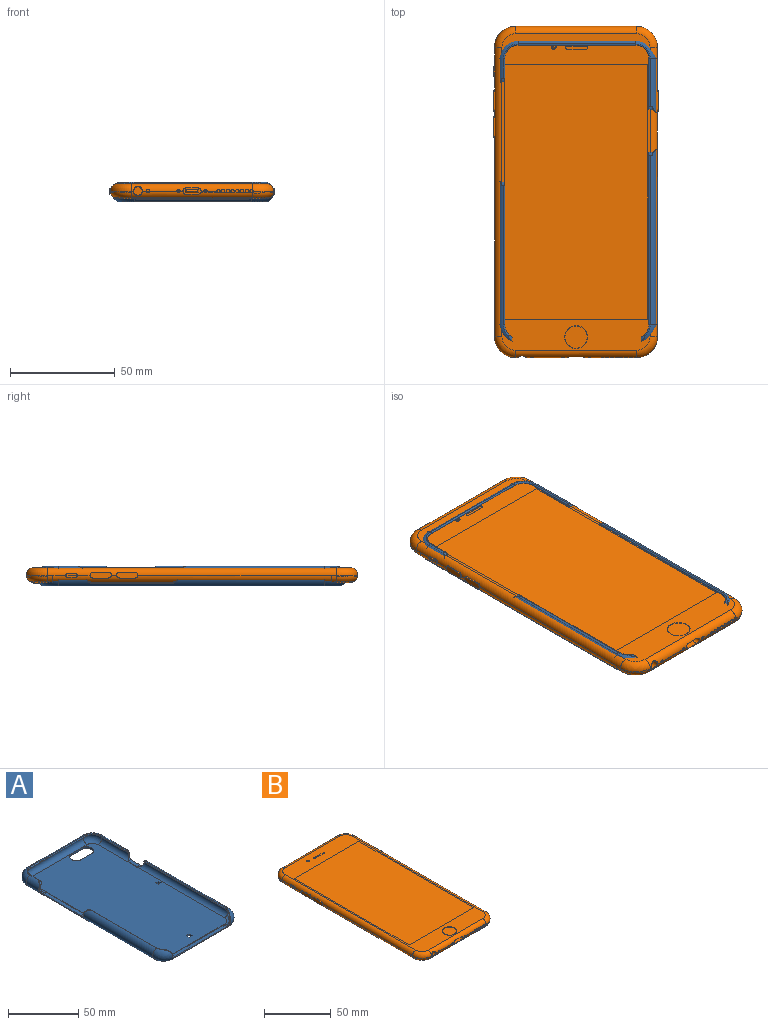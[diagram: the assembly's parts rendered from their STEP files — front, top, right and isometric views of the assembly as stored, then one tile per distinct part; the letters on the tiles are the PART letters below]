
ASSEMBLY  parts=2 mates=1
PART A: 103 faces, bbox 79x150.1x9.5 mm
  f0: cylinder r=3.5mm len=127.1mm, axis (0,1,0), area 1149.3mm2, adj f1,f8,f14,f16,f26,f53,f54,f55
  f1: cylinder r=0.5mm len=82.87mm, axis (0,1,0), area 128mm2, adj f0,f9,f15,f59,f60
  f2: cylinder r=3.5mm len=127.1mm, axis (0,1,0), area 873.9mm2, adj f3,f5,f11,f22,f26,f27,f28,f42
  f3: cylinder r=0.5mm len=11.42mm, axis (0,1,0), area 15.6mm2, adj f2,f4,f23,f46,f51
  f4: cylinder r=5mm len=127.1mm, axis (0,1,0), area 1097.8mm2, adj f3,f13,f24,f25,f27,f51,f52,f84
  f5: plane 16.43x0mm, normal (1,0,0), area 0.1mm2, adj f2,f26,f42
  f6: cylinder r=3.5mm len=56mm, axis (1,0,0), area 26.2mm2, adj f8,f11,f26,f31,f34,f35,f40,f41
  f7: cylinder r=5mm len=56mm, axis (1,0,0), area 114.5mm2, adj f10,f13,f25,f71,f72,f73
  f8: torus R=5.74mm, axis (0,0,1), area 122.4mm2, adj f0,f6,f9,f26,f29,f30,f31
  f9: torus R=6.88mm, axis (0,0,1), area 10.2mm2, adj f1,f8,f10,f29,f32,f33
  f10: torus R=5.6mm, axis (0,0,1), area 165.3mm2, adj f7,f9,f15,f25,f32,f74,f75,f76
  f11: torus R=5.74mm, axis (0,0,1), area 122.4mm2, adj f2,f6,f12,f26,f35,f36,f37
  f12: torus R=6.88mm, axis (0,0,1), area 10.2mm2, adj f11,f13,f27,f37,f38,f39
  f13: torus R=5.6mm, axis (0,0,1), area 165.3mm2, adj f4,f7,f12,f25,f38,f68,f69,f70
  f14: cylinder r=0.5mm len=24.73mm, axis (0,1,0), area 36.6mm2, adj f0,f15,f17,f53,f61
  f15: cylinder r=5mm len=127.1mm, axis (0,1,0), area 1384.9mm2, adj f1,f10,f14,f18,f25,f60,f61,f77
  f16: torus R=5.74mm, axis (0,0,1), area 129.9mm2, adj f0,f17,f19,f26
  f17: torus R=6.88mm, axis (0,0,1), area 16.2mm2, adj f14,f16,f18,f20
  f18: torus R=5.6mm, axis (0,0,1), area 182mm2, adj f15,f17,f21,f25
  f19: cylinder r=3.5mm len=56mm, axis (-1,0,0), area 572.6mm2, adj f16,f20,f22,f26,f64
  f20: cylinder r=0.5mm len=56mm, axis (-1,0,0), area 88mm2, adj f17,f19,f21,f23
  f21: cylinder r=5mm len=56mm, axis (-1,0,0), area 688.9mm2, adj f18,f20,f24,f25
  f22: torus R=5.74mm, axis (0,0,1), area 129.9mm2, adj f2,f19,f23,f26
  f23: torus R=6.88mm, axis (0,0,1), area 16.2mm2, adj f3,f20,f22,f24
  f24: torus R=5.6mm, axis (0,0,1), area 182mm2, adj f4,f21,f23,f25
  f25: plane 142.1x71mm, normal (0,0,-1), area 9834.1mm2, adj f4,f7,f10,f13,f15,f18,f21,f24
  f26: plane 138.18x67.14mm, normal (0,0,1), area 9026.4mm2, adj f0,f2,f5,f6,f8,f11,f16,f19
  f27: cylinder r=0.5mm len=68.7mm, axis (0,1,0), area 105.6mm2, adj f2,f4,f12,f47,f52
  f28: plane 73.67x0mm, normal (1,0,0), area 0.3mm2, adj f2,f26,f43
  f29: cylinder r=3.5mm len=4.97mm, axis (0,1,0), area 7.4mm2, adj f8,f9,f30,f32,f33,f76
  f30: plane 1.06x0.55mm, normal (-1,0,0), area 0.5mm2, adj f8,f29,f31,f75
  f31: cylinder r=3.5mm len=4.29mm, axis (0,1,0), area 9.6mm2, adj f6,f8,f30,f34,f73,f74
  f32: plane 1.34x0.37mm, normal (-1,0,0), area 0.2mm2, adj f9,f10,f29,f33,f76
  f33: plane 0.66x0.4mm, normal (0,-1,0), area 0.1mm2, adj f9,f29,f32
  f34: plane 50.8x3.01mm, normal (0,0,1), area 152.9mm2, adj f6,f31,f35,f72
  f35: cylinder r=3.5mm len=4.29mm, axis (0,1,0), area 9.6mm2, adj f6,f11,f34,f36,f70,f71
  f36: plane 1.06x0.55mm, normal (1,0,0), area 0.5mm2, adj f11,f35,f37,f69
  f37: cylinder r=3.5mm len=4.97mm, axis (0,1,0), area 7.4mm2, adj f11,f12,f36,f38,f39,f68
  f38: plane 1.34x0.37mm, normal (1,0,0), area 0.2mm2, adj f12,f13,f37,f39,f68
  f39: plane 0.66x0.4mm, normal (0,-1,0), area 0.1mm2, adj f12,f37,f38
  f40: cylinder r=3.5mm len=0.17mm, axis (0,1,0), area 0mm2, adj f6,f26
  f41: cylinder r=3.5mm len=0.17mm, axis (0,1,0), area 0mm2, adj f6,f26
  f42: cylinder r=3.5mm len=0.17mm, axis (-1,0,0), area 0mm2, adj f2,f5,f26
  f43: cylinder r=3.5mm len=0.17mm, axis (-1,0,0), area 0mm2, adj f2,f26,f28
  f44: plane 37x3.01mm, normal (0,0,1), area 111.4mm2, adj f2,f49,f50,f87
  f45: plane 1.06x0.47mm, normal (0,-1,0), area 0.5mm2, adj f2,f46,f49,f89
  f46: cylinder r=3.5mm len=3.8mm, axis (-1,0,0), area 8.6mm2, adj f2,f3,f45,f51,f90
  f47: cylinder r=3.5mm len=3.8mm, axis (-1,0,0), area 8.6mm2, adj f2,f27,f48,f52,f84
  f48: plane 1.09x0.97mm, normal (0,1,0), area 1mm2, adj f2,f47,f50,f85
  f49: cylinder r=3.5mm len=4.36mm, axis (-1,0,0), area 8.9mm2, adj f2,f44,f45,f88
  f50: cylinder r=3.5mm len=4.38mm, axis (-1,0,0), area 10.2mm2, adj f2,f44,f48,f86
  f51: plane 1.53x0.39mm, normal (0,-1,0), area 0.3mm2, adj f3,f4,f46,f90
  f52: plane 1.53x0.39mm, normal (0,1,0), area 0.3mm2, adj f4,f27,f47,f84
  f53: cylinder r=3.5mm len=3.85mm, axis (1,0,0), area 9mm2, adj f0,f14,f54,f61,f77
  f54: plane 1.05x0.32mm, normal (0,-1,0), area 0.3mm2, adj f0,f53,f55,f78
  f55: cylinder r=3.5mm len=4.36mm, axis (1,0,0), area 8.9mm2, adj f0,f54,f56,f79
  f56: plane 9x3.01mm, normal (0,0,1), area 27.1mm2, adj f0,f55,f57,f80
  f57: cylinder r=3.5mm len=4.36mm, axis (1,0,0), area 8.9mm2, adj f0,f56,f58,f81
  f58: plane 1.05x0.32mm, normal (0,1,0), area 0.3mm2, adj f0,f57,f59,f82
  f59: cylinder r=3.5mm len=3.85mm, axis (1,0,0), area 9mm2, adj f0,f1,f58,f60,f83
  f60: plane 1.84x0.56mm, normal (0,1,0), area 0.6mm2, adj f1,f15,f59,f83
  f61: plane 1.84x0.56mm, normal (0,-1,0), area 0.6mm2, adj f14,f15,f53,f77
  f62: cylinder r=3.5mm len=0.17mm, axis (1,0,0), area 0mm2, adj f0,f26
  f63: cylinder r=3.5mm len=0.17mm, axis (1,0,0), area 0mm2, adj f0,f26
  f64: plane 10.12x1.61mm, normal (0,-1,0), area 16.2mm2, adj f19,f25,f65,f67
  f65: cylinder r=5mm len=10mm, axis (0,0,1), area 25.1mm2, adj f25,f26,f64,f66
  f66: plane 10.11x1.6mm, normal (0,1,0), area 16.2mm2, adj f25,f26,f65,f67
  f67: cylinder r=5mm len=10mm, axis (0,0,1), area 25.1mm2, adj f25,f26,f64,f66
  f68: bspline ~4.29x3.86mm, area 2.1mm2, adj f13,f37,f38,f69
  f69: bspline ~0.6x0.38mm, area 0.2mm2, adj f13,f36,f68,f70
  f70: bspline ~2.94x1.44mm, area 1.4mm2, adj f13,f35,f69,f71
  f71: bspline ~2.6x1.46mm, area 1.5mm2, adj f7,f35,f70,f72
  f72: plane 50.8x0.51mm, normal (0,-0.92,0.38), area 28mm2, adj f7,f34,f71,f73
  f73: bspline ~2.6x1.46mm, area 1.5mm2, adj f7,f31,f72,f74
  f74: bspline ~2.94x1.45mm, area 1.4mm2, adj f10,f31,f73,f75
  f75: bspline ~0.6x0.38mm, area 0.2mm2, adj f10,f30,f74,f76
  f76: bspline ~4.29x3.86mm, area 2.1mm2, adj f10,f29,f32,f75
  f77: bspline ~3.8x3.54mm, area 1.8mm2, adj f15,f53,f61,f78
  f78: cone r=4.7mm half-angle=45deg, axis (0,1,0), area 0.1mm2, adj f15,f54,f77,f79
  f79: bspline ~4.04x3.8mm, area 2.9mm2, adj f15,f55,f78,f80
  f80: plane 9x0.51mm, normal (0.92,0,0.38), area 5mm2, adj f15,f56,f79,f81
  f81: bspline ~4.04x3.8mm, area 2.9mm2, adj f15,f57,f80,f82
  f82: cone r=4.7mm half-angle=45deg, axis (0,-1,0), area 0.1mm2, adj f15,f58,f81,f83
  f83: bspline ~3.5x3.5mm, area 1.8mm2, adj f15,f59,f60,f82
  f84: bspline ~3.81x3.54mm, area 1.7mm2, adj f4,f47,f52,f85
  f85: cone r=5mm half-angle=45deg, axis (0,-1,0), area 0.4mm2, adj f4,f48,f84,f86
  f86: bspline ~3.79x3.79mm, area 2.7mm2, adj f4,f50,f85,f87
  f87: plane 37x0.51mm, normal (-0.92,0,0.38), area 20.4mm2, adj f4,f44,f86,f88
  f88: bspline ~4.04x3.8mm, area 2.9mm2, adj f4,f49,f87,f89
  f89: cone r=5mm half-angle=45deg, axis (0,1,0), area 0.2mm2, adj f4,f45,f88,f90
  f90: bspline ~3.81x3.54mm, area 1.7mm2, adj f4,f46,f51,f89
  f91: plane 3x1.6mm, normal (0,-1,0), area 4.8mm2, adj f25,f26,f92,f93
  f92: plane 3x1.6mm, normal (-1,0,0), area 4.8mm2, adj f25,f26,f91,f94
  f93: plane 3x1.6mm, normal (1,0,0), area 4.8mm2, adj f25,f26,f91,f94
  f94: plane 3x1.6mm, normal (0,1,0), area 4.8mm2, adj f25,f26,f92,f93
  f95: plane 3x1.6mm, normal (0,-1,0), area 4.8mm2, adj f25,f26,f96,f97
  f96: plane 3x1.6mm, normal (-1,0,0), area 4.8mm2, adj f25,f26,f95,f98
  f97: plane 3x1.6mm, normal (1,0,0), area 4.8mm2, adj f25,f26,f95,f98
  f98: plane 3x1.6mm, normal (0,1,0), area 4.8mm2, adj f25,f26,f96,f97
  f99: plane 3x1.6mm, normal (-1,0,0), area 4.8mm2, adj f25,f26,f100,f101
  f100: plane 3x1.6mm, normal (0,1,0), area 4.8mm2, adj f25,f26,f99,f102
  f101: plane 3x1.6mm, normal (0,-1,0), area 4.8mm2, adj f25,f26,f99,f102
  f102: plane 3x1.6mm, normal (1,0,0), area 4.8mm2, adj f25,f26,f100,f101
PART B: 184 faces, bbox 79.4x159.7x7.8 mm
  f0: cylinder r=3.55mm len=3.55mm, axis (0,1,0), area 12.2mm2, adj f2,f5,f6,f32,f62
  f1: cylinder r=3.55mm len=3.55mm, axis (0,-1,0), area 12.2mm2, adj f2,f4,f7,f36,f59
  f2: plane 70.69x1.5mm, normal (0,0,-1), area 106mm2, adj f0,f1,f8,f39
  f3: cylinder r=3.55mm len=57.79mm, axis (-1,0,0), area 154.9mm2, adj f4,f5,f9,f10,f11,f12,f13,f14
  f4: torus R=6.45mm, axis (0,0,-1), area 41.5mm2, adj f1,f3,f22,f23,f49,f50
  f5: torus R=6.45mm, axis (0,0,-1), area 42.1mm2, adj f0,f3,f24,f25,f69
  f6: cylinder r=3.55mm len=132.83mm, axis (0,1,0), area 710.8mm2, adj f0,f8,f28,f62,f78,f79,f81,f83
  f7: cylinder r=3.55mm len=132.83mm, axis (0,-1,0), area 709.9mm2, adj f1,f8,f27,f59,f74,f99,f100,f101
  f8: plane 132.83x70.69mm, normal (0,0,-1), area 9132.5mm2, adj f2,f6,f7,f26,f48,f65
  f9: cylinder r=3.55mm len=0.95mm, axis (-1,0,0), area 0.1mm2, adj f3,f43,f148
  f10: cylinder r=3.55mm len=2mm, axis (-1,0,0), area 0.4mm2, adj f3,f43,f56,f148
  f11: cylinder r=3.55mm len=13.09mm, axis (-1,0,0), area 4.2mm2, adj f3,f40,f43,f56
  f12: cylinder r=3.55mm len=1.41mm, axis (-1,0,0), area 0.5mm2, adj f3,f40,f43,f109
  f13: cylinder r=3.55mm len=1.49mm, axis (-1,0,0), area 0.7mm2, adj f3,f43,f44,f111
  f14: cylinder r=3.55mm len=5.01mm, axis (-1,0,0), area 2.5mm2, adj f3,f43,f44,f131
  f15: cylinder r=3.55mm len=1.06mm, axis (-1,0,0), area 0.5mm2, adj f3,f43,f129,f131
  f16: cylinder r=3.55mm len=1.09mm, axis (-1,0,0), area 0.5mm2, adj f3,f43,f127,f129
  f17: cylinder r=3.55mm len=1.12mm, axis (-1,0,0), area 0.5mm2, adj f3,f43,f125,f127
  f18: cylinder r=3.55mm len=1.14mm, axis (-1,0,0), area 0.5mm2, adj f3,f43,f123,f125
  f19: cylinder r=3.55mm len=1.17mm, axis (-1,0,0), area 0.5mm2, adj f3,f43,f121,f123
  f20: cylinder r=3.55mm len=1.2mm, axis (-1,0,0), area 0.6mm2, adj f3,f43,f119,f121
  f21: cylinder r=3.55mm len=1.23mm, axis (-1,0,0), area 0.6mm2, adj f3,f43,f117,f119
  f22: torus R=6.45mm, axis (0,0,-1), area 4.3mm2, adj f4,f50
  f23: torus R=6.45mm, axis (0,0,-1), area 5.8mm2, adj f4,f50,f117
  f24: torus R=6.45mm, axis (0,0,-1), area 4.7mm2, adj f5,f72
  f25: torus R=6.45mm, axis (0,0,-1), area 4.7mm2, adj f5,f72
  f26: plane 70.69x1.5mm, normal (0,0,-1), area 106mm2, adj f8,f27,f28,f47
  f27: cylinder r=3.55mm len=3.55mm, axis (0,-1,0), area 12.2mm2, adj f7,f26,f31,f58,f59
  f28: cylinder r=3.55mm len=3.55mm, axis (0,1,0), area 12.1mm2, adj f6,f26,f29,f33,f61,f62
  f29: torus R=6.45mm, axis (0,0,-1), area 42.4mm2, adj f28,f30,f34,f35,f66,f67
  f30: cylinder r=3.55mm len=57.79mm, axis (1,0,0), area 196mm2, adj f29,f31,f68,f70
  f31: torus R=6.45mm, axis (0,0,-1), area 42.1mm2, adj f27,f30,f37,f38,f71
  f32: cylinder r=3.55mm len=2.05mm, axis (0,1,0), area 2.4mm2, adj f0,f39,f69
  f33: cylinder r=3.55mm len=0.28mm, axis (0,1,0), area 0mm2, adj f28,f34,f62
  f34: torus R=6.45mm, axis (0,0,-1), area 3.4mm2, adj f29,f33,f67
  f35: torus R=6.45mm, axis (0,0,-1), area 5.7mm2, adj f29,f67
  f36: cylinder r=3.55mm len=2.05mm, axis (0,-1,0), area 2.4mm2, adj f1,f39,f49
  f37: torus R=6.45mm, axis (0,0,-1), area 4.7mm2, adj f31,f73
  f38: torus R=6.45mm, axis (0,0,-1), area 4.7mm2, adj f31,f73
  f39: plane 70.69x7.57mm, normal (0,0,-1), area 517.3mm2, adj f2,f32,f36,f42,f49,f69
  f40: cylinder r=3.55mm len=1.6mm, axis (-1,0,0), area 0.8mm2, adj f3,f11,f12,f41,f168,f169,f170,f171
  f41: cylinder r=3.55mm len=1.6mm, axis (1,0,0), area 0.9mm2, adj f40,f43,f163,f164,f165,f166,f167,f168
  f42: cylinder r=3.55mm len=57.79mm, axis (-1,0,0), area 124.3mm2, adj f3,f39,f49,f69
  f43: cylinder r=3.55mm len=57.79mm, axis (1,0,0), area 290.7mm2, adj f9,f10,f11,f12,f13,f14,f15,f16
  f44: cylinder r=3.55mm len=1.6mm, axis (-1,0,0), area 0.8mm2, adj f3,f13,f14,f45,f153,f154,f155,f156
  f45: cylinder r=3.55mm len=1.6mm, axis (1,0,0), area 0.9mm2, adj f43,f44,f150,f151,f152,f153,f159,f160
  f46: plane 1.5x1.5mm, normal (0,0,1), area 1mm2, adj f142,f143
  f47: plane 70.69x7.57mm, normal (0,0,-1), area 456.1mm2, adj f26,f58,f61,f66,f68,f71,f104,f144
  f48: plane 18.21x17.51mm, normal (0,0,-1), area 242.8mm2, adj f8
  f49: torus R=6.45mm, axis (0,0,-1), area 24.6mm2, adj f4,f36,f39,f42
  f50: torus R=6.45mm, axis (0,0,-1), area 76.2mm2, adj f4,f22,f23,f43,f59,f63,f117
  f51: cylinder r=1.7mm len=1.7mm, axis (0,0,-1), area 1.5mm2, adj f52,f54,f113
  f52: cylinder r=1.7mm len=6.5mm, axis (1,0,0), area 10.1mm2, adj f51,f53,f54,f114
  f53: cylinder r=1.7mm len=1.7mm, axis (0,0,1), area 1.5mm2, adj f52,f54,f115
  f54: cylinder r=1.7mm len=6.5mm, axis (-1,0,0), area 10.1mm2, adj f51,f52,f53,f116
  f55: plane 8.7x2.95mm, normal (0,-1,0), area 12.7mm2, adj f109,f110,f111,f112,f113,f114,f115,f116
  f56: cylinder r=3.55mm len=1.6mm, axis (-1,0,0), area 1mm2, adj f3,f10,f11,f57
  f57: cylinder r=3.55mm len=1.6mm, axis (1,0,0), area 1mm2, adj f43,f56
  f58: cylinder r=3.55mm len=2.05mm, axis (0,-1,0), area 2.4mm2, adj f27,f47,f71
  f59: cylinder r=3.55mm len=138.07mm, axis (0,1,0), area 739.1mm2, adj f1,f7,f27,f50,f63,f73,f75,f98
  f60: plane 5.61x1.96mm, normal (-1,0,0), area 5.5mm2, adj f88,f89,f90,f91,f92,f93,f94,f95
  f61: cylinder r=3.55mm len=2.09mm, axis (0,1,0), area 2.5mm2, adj f28,f47,f66
  f62: cylinder r=3.55mm len=138.07mm, axis (0,-1,0), area 737.2mm2, adj f0,f6,f28,f33,f63,f67,f72,f79
  f63: plane 150.97x70.69mm, normal (0,0,1), area 2217.1mm2, adj f43,f50,f59,f62,f64,f67,f70,f72
  f64: plane 121.54x68.36mm, normal (0,0,1), area 8308.5mm2, adj f63
  f65: plane 5.18x4.88mm, normal (0,0,-1), area 13.6mm2, adj f8
  f66: torus R=6.45mm, axis (0,0,-1), area 24.8mm2, adj f29,f47,f61,f68
  f67: torus R=6.45mm, axis (0,0,-1), area 76.3mm2, adj f29,f34,f35,f62,f63,f70
  f68: cylinder r=3.55mm len=57.79mm, axis (1,0,0), area 126.3mm2, adj f30,f47,f66,f71,f106
  f69: torus R=6.45mm, axis (0,0,-1), area 24.8mm2, adj f5,f32,f39,f42
  f70: cylinder r=3.55mm len=57.79mm, axis (-1,0,0), area 322.3mm2, adj f30,f63,f67,f73
  f71: torus R=6.45mm, axis (0,0,-1), area 24.8mm2, adj f31,f47,f58,f68
  f72: torus R=6.45mm, axis (0,0,-1), area 76.3mm2, adj f24,f25,f43,f62,f63
  f73: torus R=6.45mm, axis (0,0,-1), area 76.3mm2, adj f37,f38,f59,f63,f70
  f74: cylinder r=3.55mm len=15.81mm, axis (0,-1,0), area 17.2mm2, adj f7,f75,f102
  f75: cylinder r=3.55mm len=15.81mm, axis (0,1,0), area 16.6mm2, adj f59,f74,f102
  f76: cone r=5.45mm half-angle=45deg, axis (0,0,1), area 7.2mm2, adj f63,f77
  f77: plane 10.6x10.6mm, normal (0,0,1), area 88.2mm2, adj f76
  f78: plane 7.4x0.59mm, normal (0,0,-1), area 4.3mm2, adj f6,f79,f81,f82
  f79: cylinder r=1.4mm len=2.8mm, axis (-1,0,0), area 2mm2, adj f6,f62,f78,f80,f82
  f80: plane 7.4x0.59mm, normal (0,0,1), area 4.3mm2, adj f62,f79,f81,f82
  f81: cylinder r=1.4mm len=2.8mm, axis (-1,0,0), area 2mm2, adj f6,f62,f78,f80,f82
  f82: plane 10.2x2.8mm, normal (-1,0,0), area 26.9mm2, adj f78,f79,f80,f81
  f83: plane 7.4x0.59mm, normal (0,0,-1), area 4.3mm2, adj f6,f84,f86,f87
  f84: cylinder r=1.4mm len=2.8mm, axis (-1,0,0), area 2mm2, adj f6,f62,f83,f85,f87
  f85: plane 7.4x0.59mm, normal (0,0,1), area 4.3mm2, adj f62,f84,f86,f87
  f86: cylinder r=1.4mm len=2.8mm, axis (-1,0,0), area 2mm2, adj f6,f62,f83,f85,f87
  f87: plane 10.2x2.8mm, normal (-1,0,0), area 26.9mm2, adj f83,f84,f85,f86
  f88: cylinder r=0.98mm len=1.96mm, axis (-1,0,0), area 1.3mm2, adj f6,f60,f62,f89,f91
  f89: plane 3.65x0.36mm, normal (0,0,-1), area 1.3mm2, adj f60,f62,f88,f90
  f90: cylinder r=0.98mm len=1.96mm, axis (-1,0,0), area 1.3mm2, adj f6,f60,f62,f89,f91
  f91: plane 3.65x0.36mm, normal (0,0,1), area 1.3mm2, adj f6,f60,f88,f90
  f92: cylinder r=0.47mm len=0.93mm, axis (1,0,0), area 1.2mm2, adj f60,f93,f95,f96
  f93: plane 4.31x0.8mm, normal (0,0,-1), area 3.4mm2, adj f60,f92,f94,f96
  f94: cylinder r=0.47mm len=0.93mm, axis (1,0,0), area 1.2mm2, adj f60,f93,f95,f96
  f95: plane 4.31x0.8mm, normal (0,0,1), area 3.4mm2, adj f60,f92,f94,f96
  f96: plane 5.24x0.93mm, normal (-1,0,0), area 4.7mm2, adj f92,f93,f94,f95
  f97: plane 10.2x2.8mm, normal (1,0,0), area 26.9mm2, adj f98,f99,f100,f101
  f98: plane 7.4x0.59mm, normal (0,0,1), area 4.3mm2, adj f59,f97,f99,f101
  f99: cylinder r=1.4mm len=2.8mm, axis (1,0,0), area 2mm2, adj f7,f59,f97,f98,f100
  f100: plane 7.4x0.59mm, normal (0,0,-1), area 4.3mm2, adj f7,f97,f99,f101
  f101: cylinder r=1.4mm len=2.8mm, axis (1,0,0), area 2mm2, adj f7,f59,f97,f98,f100
  f102: cylinder r=1mm len=2mm, axis (1,0,0), area 7.3mm2, adj f74,f75,f103
  f103: plane 2x2mm, normal (1,0,0), area 3.1mm2, adj f102
  f104: cylinder r=3.83mm len=7.66mm, axis (0,0,1), area 16.1mm2, adj f47,f105,f106
  f105: plane 7.66x7.66mm, normal (0,0,-1), area 46.1mm2, adj f104
  f106: plane 2.32x0.18mm, normal (0,0,1), area 0.3mm2, adj f68,f104
  f107: cylinder r=2.02mm len=9.64mm, axis (0,-1,0), area 117.8mm2, adj f108,f148,f149
  f108: plane 4.05x4.05mm, normal (0,-1,0), area 12.9mm2, adj f107
  f109: cylinder r=1.47mm len=5mm, axis (0,-1,0), area 22.5mm2, adj f3,f12,f43,f55,f110,f112
  f110: plane 5.75x4.68mm, normal (0,0,-1), area 26.9mm2, adj f43,f55,f109,f111
  f111: cylinder r=1.47mm len=5mm, axis (0,-1,0), area 22.5mm2, adj f3,f13,f43,f55,f110,f112
  f112: plane 5.75x4.68mm, normal (0,0,1), area 26.9mm2, adj f3,f55,f109,f111
  f113: plane 1.7x0.8mm, normal (1,0,0), area 1.4mm2, adj f51,f55,f114,f116
  f114: plane 6.5x0.8mm, normal (0,0,1), area 5.2mm2, adj f52,f55,f113,f115
  f115: plane 1.7x0.8mm, normal (-1,0,0), area 1.4mm2, adj f53,f55,f114,f116
  f116: plane 6.5x0.8mm, normal (0,0,-1), area 5.2mm2, adj f54,f55,f113,f115
  f117: cylinder r=0.8mm len=1.6mm, axis (0,-1,0), area 4.9mm2, adj f3,f21,f23,f43,f50,f118
  f118: plane 1.6x1.6mm, normal (0,-1,0), area 2mm2, adj f117
  f119: cylinder r=0.8mm len=1.6mm, axis (0,-1,0), area 4.9mm2, adj f3,f20,f21,f43,f120
  f120: plane 1.6x1.6mm, normal (0,-1,0), area 2mm2, adj f119
  f121: cylinder r=0.8mm len=1.6mm, axis (0,-1,0), area 4.9mm2, adj f3,f19,f20,f43,f122
  f122: plane 1.6x1.6mm, normal (0,-1,0), area 2mm2, adj f121
  f123: cylinder r=0.8mm len=1.6mm, axis (0,-1,0), area 4.9mm2, adj f3,f18,f19,f43,f124
  f124: plane 1.6x1.6mm, normal (0,-1,0), area 2mm2, adj f123
  f125: cylinder r=0.8mm len=1.6mm, axis (0,-1,0), area 4.9mm2, adj f3,f17,f18,f43,f126
  f126: plane 1.6x1.6mm, normal (0,-1,0), area 2mm2, adj f125
  f127: cylinder r=0.8mm len=1.6mm, axis (0,-1,0), area 4.9mm2, adj f3,f16,f17,f43,f128
  f128: plane 1.6x1.6mm, normal (0,-1,0), area 2mm2, adj f127
  f129: cylinder r=0.8mm len=1.6mm, axis (0,-1,0), area 4.9mm2, adj f3,f15,f16,f43,f130
  f130: plane 1.6x1.6mm, normal (0,-1,0), area 2mm2, adj f129
  f131: cylinder r=0.8mm len=1.6mm, axis (0,-1,0), area 4.9mm2, adj f3,f14,f15,f43,f132
  f132: plane 1.6x1.6mm, normal (0,-1,0), area 2mm2, adj f131
  f133: cylinder r=0.6mm len=1.2mm, axis (0,0,1), area 0.2mm2, adj f63,f134,f136,f137
  f134: plane 9.5x0.1mm, normal (0,-1,0), area 1mm2, adj f63,f133,f135,f137
  f135: cylinder r=0.6mm len=1.2mm, axis (0,0,1), area 0.2mm2, adj f63,f134,f136,f137
  f136: plane 9.5x0.1mm, normal (0,1,0), area 1mm2, adj f63,f133,f135,f137
  f137: plane 10.7x1.2mm, normal (0,0,1), area 12.5mm2, adj f133,f134,f135,f136
  f138: cylinder r=1.25mm len=2.5mm, axis (0,0,1), area 2mm2, adj f63,f139
  f139: plane 2.5x2.5mm, normal (0,0,1), area 1.8mm2, adj f138,f140
  f140: cylinder r=1mm len=2mm, axis (0,0,1), area 1.6mm2, adj f139,f141
  f141: plane 2x2mm, normal (0,0,1), area 1.4mm2, adj f140,f142
  f142: cylinder r=0.75mm len=1.5mm, axis (0,0,1), area 1.2mm2, adj f46,f141
  f143: sphere r=0.5mm, area 1.6mm2, adj f46
  f144: cylinder r=2.06mm len=4.11mm, axis (0,0,1), area 0.6mm2, adj f47,f145
  f145: plane 4.11x4.11mm, normal (0,0,-1), area 13.3mm2, adj f144
  f146: cylinder r=0.8mm len=1.6mm, axis (0,0,-1), area 0.5mm2, adj f47,f147
  f147: plane 1.6x1.6mm, normal (0,0,-1), area 2mm2, adj f146
  f148: bspline ~4.23x2.35mm, area 2.8mm2, adj f3,f9,f10,f107,f149
  f149: bspline ~4.23x2.35mm, area 2.8mm2, adj f43,f107,f148
  f150: plane 0.2x0.17mm, normal (0,0,-1), area 0mm2, adj f45,f151,f161,f162
  f151: plane 0.35x0.2mm, normal (-1,0,0), area 0.1mm2, adj f45,f150,f152,f162
  f152: plane 0.35x0.2mm, normal (0,0,-1), area 0.1mm2, adj f45,f151,f153,f162
  f153: plane 0.2x0.2mm, normal (-1,0,0), area 0mm2, adj f44,f45,f152,f154,f162
  f154: plane 0.35x0.2mm, normal (0,0,1), area 0.1mm2, adj f44,f153,f155,f162
  f155: plane 0.35x0.2mm, normal (-1,0,0), area 0.1mm2, adj f44,f154,f156,f162
  f156: plane 0.2x0.17mm, normal (0,0,1), area 0mm2, adj f44,f155,f157,f162
  f157: plane 0.35x0.2mm, normal (1,0,0), area 0.1mm2, adj f44,f156,f158,f162
  f158: plane 0.35x0.2mm, normal (0,0,1), area 0.1mm2, adj f44,f157,f159,f162
  f159: plane 0.2x0.2mm, normal (1,0,0), area 0mm2, adj f44,f45,f158,f160,f162
  f160: plane 0.35x0.2mm, normal (0,0,-1), area 0.1mm2, adj f45,f159,f161,f162
  f161: plane 0.35x0.2mm, normal (1,0,0), area 0.1mm2, adj f45,f150,f160,f162
  f162: plane 0.9x0.9mm, normal (0,-1,0), area 0.3mm2, adj f150,f151,f152,f153,f154,f155,f156,f157
  f163: plane 0.35x0.2mm, normal (0,0,-1), area 0.1mm2, adj f41,f164,f174,f175
  f164: plane 0.35x0.2mm, normal (-1,0,0), area 0.1mm2, adj f41,f163,f165,f175
  f165: plane 0.2x0.17mm, normal (0,0,-1), area 0mm2, adj f41,f164,f166,f175
  f166: plane 0.35x0.2mm, normal (1,0,0), area 0.1mm2, adj f41,f165,f167,f175
  f167: plane 0.35x0.2mm, normal (0,0,-1), area 0.1mm2, adj f41,f166,f168,f175
  f168: plane 0.2x0.2mm, normal (1,0,0), area 0mm2, adj f40,f41,f167,f169,f175
  f169: plane 0.35x0.2mm, normal (0,0,1), area 0.1mm2, adj f40,f168,f170,f175
  f170: plane 0.35x0.2mm, normal (1,0,0), area 0.1mm2, adj f40,f169,f171,f175
  f171: plane 0.2x0.17mm, normal (0,0,1), area 0mm2, adj f40,f170,f172,f175
  f172: plane 0.35x0.2mm, normal (-1,0,0), area 0.1mm2, adj f40,f171,f173,f175
  f173: plane 0.35x0.2mm, normal (0,0,1), area 0.1mm2, adj f40,f172,f174,f175
  f174: plane 0.2x0.2mm, normal (-1,0,0), area 0mm2, adj f40,f41,f163,f173,f175
  f175: plane 0.9x0.9mm, normal (0,-1,0), area 0.3mm2, adj f163,f164,f165,f166,f167,f168,f169,f170
  f176: plane 6.9x6.9mm, normal (0,0,1), area 37.4mm2, adj f183
  f177: sphere r=1.52mm, area 4.8mm2, adj f178
  f178: cylinder r=1.12mm len=2.25mm, axis (0,0,-1), area 3.5mm2, adj f177,f179
  f179: plane 2.75x2.75mm, normal (0,0,-1), area 2mm2, adj f178,f180
  f180: plane 3.75x3.75mm, normal (0,0,-1), area 5.1mm2, adj f179,f181
  f181: cylinder r=1.88mm len=3.75mm, axis (0,0,-1), area 11.8mm2, adj f180,f182
  f182: plane 6.9x6.9mm, normal (0,0,-1), area 26.3mm2, adj f181,f183
  f183: cylinder r=3.45mm len=6.9mm, axis (0,0,-1), area 1.1mm2, adj f176,f182
PLACE A rot(axis=(0,0,1),0deg) t=(16.47,42.72,30.55)mm fixed
PLACE B rot(axis=(0,0,1),0deg) t=(16.1,42.64,30.55)mm
MATE slider B.f8 <-> A.f26  axis (0,0,-1) through (16.12,41.49,30.55)mm
